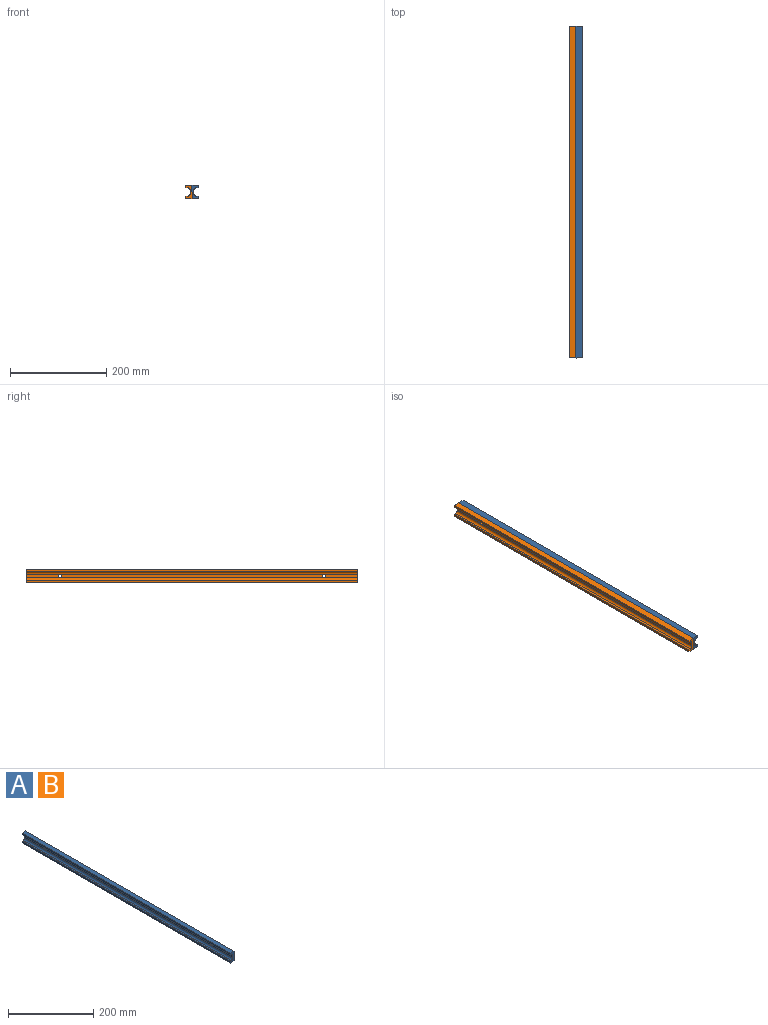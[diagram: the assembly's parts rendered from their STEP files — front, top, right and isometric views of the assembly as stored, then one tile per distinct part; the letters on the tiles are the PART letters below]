
ASSEMBLY  parts=2 mates=1
PART A: 14 faces, bbox 13x690.6x28 mm
  f0: plane 690.56x7.7mm, normal (-1,0,0), area 5230.5mm2, adj f8,f9,f10,f11,f12,f13
  f1: plane 690.56x28mm, normal (1,0,0), area 19252.1mm2, adj f2,f7,f8,f9,f12,f13
  f2: plane 690.56x13.01mm, normal (0,0,1), area 8980.6mm2, adj f1,f3,f8,f9
  f3: plane 690.56x5.08mm, normal (-1,0,0), area 3508.1mm2, adj f2,f4,f8,f9
  f4: plane 690.56x4.1mm, normal (0,0,-1), area 2832.8mm2, adj f3,f8,f9,f10
  f5: plane 690.56x4.1mm, normal (0,0,1), area 2832.8mm2, adj f6,f8,f9,f11
  f6: plane 690.56x5.08mm, normal (-1,0,0), area 3508.1mm2, adj f5,f7,f8,f9
  f7: plane 690.56x13.01mm, normal (0,0,-1), area 8980.6mm2, adj f1,f6,f8,f9
  f8: plane 28x13.01mm, normal (0,-1,0), area 216.3mm2, adj f0,f1,f2,f3,f4,f5,f6,f7
  f9: plane 28x13.01mm, normal (0,1,0), area 216.3mm2, adj f0,f1,f2,f3,f4,f5,f6,f7
  f10: cylinder r=5.08mm len=690.56mm, axis (0,1,0), area 5317.4mm2, adj f0,f4,f8,f9
  f11: cylinder r=5.08mm len=690.56mm, axis (0,1,0), area 5317.4mm2, adj f0,f5,f8,f9
  f12: cylinder r=3.65mm len=7.3mm, axis (1,0,0), area 94mm2, adj f0,f1
  f13: cylinder r=3.65mm len=7.3mm, axis (1,0,0), area 94mm2, adj f0,f1
PART B: same geometry as A
PLACE A rot(axis=(0,1,0),180deg) t=(-196.98,237.3,-11.35)mm
PLACE B rot(axis=(0,-1,0),0deg) t=(-209.98,237.3,28.42)mm
MATE parallel A.f1 <-> B.f1  axis (-1,0,0) through (-203.48,-107.98,8.53)mm
